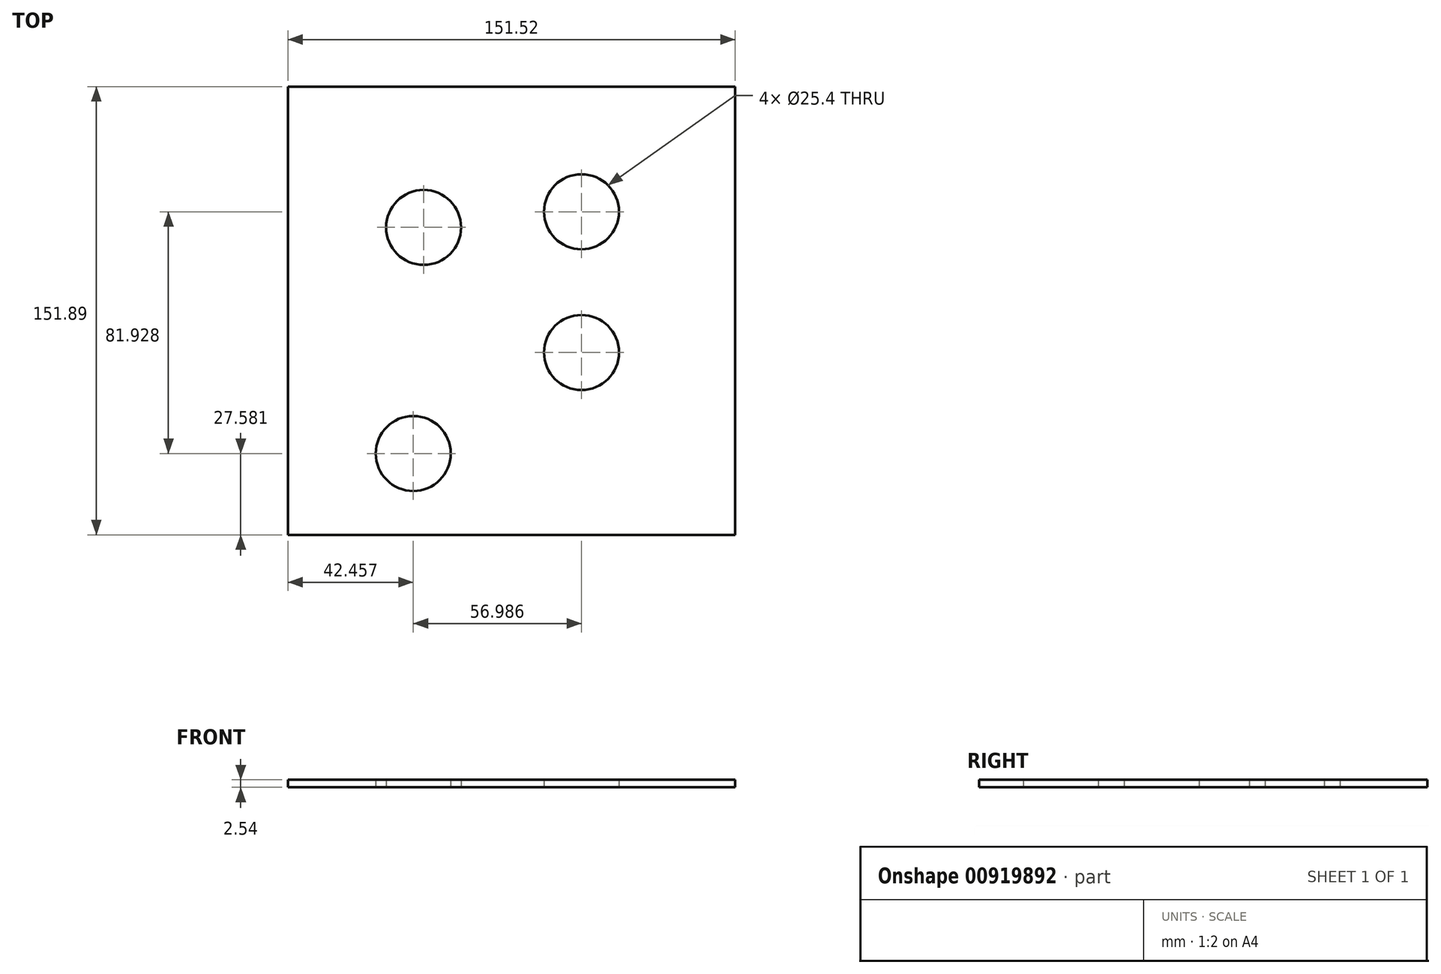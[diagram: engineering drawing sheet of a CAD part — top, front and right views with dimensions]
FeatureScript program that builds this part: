
annotation { "Feature Type Name" : "Feature", "Feature Type Description" : "" }
export const myFeature = defineFeature(function(context is Context, id is Id, definition is map)
    precondition{}
    {
        {
            var Q0;
            Q0=qCreatedBy(makeId("Top.planeOp"),FACE);
            var sketch = newSketch(context, id + "F0", { "sketchPlane" : qUnion([Q0])});
            skLineSegment(sketch, "E0.bottom", {"start": v(-75.39, 75.39) * mm, "end": v(76.13, 75.39) * mm});
            skLineSegment(sketch, "E0.top", {"start": v(-75.39, -76.5) * mm, "end": v(76.13, -76.5) * mm});
            skLineSegment(sketch, "E0.left", {"start": v(-75.39, 75.39) * mm, "end": v(-75.39, -76.5) * mm});
            skLineSegment(sketch, "E0.right", {"start": v(76.13, 75.39) * mm, "end": v(76.13, -76.5) * mm});
            skSolve(sketch);
        }
        {
            var Q0;
            Q0 = qSketchRegion(id + "F0", true);
            extrude(context, id + "F1", {"entities" : qUnion([Q0]), "depth" : 2.54 * mm, "offsetDistance" : 25.4 * mm});
        }
        {
            var Q0;
            Q0=makeQuery(id+"F1.opExtrude","CAP_FACE",FACE,{"disambiguationData":[OSD([sQuery(id+"F0.wireOp",EDGE,"E0.bottom"),sQuery(id+"F0.wireOp",EDGE,"E0.top"),sQuery(id+"F0.wireOp",EDGE,"E0.left"),sQuery(id+"F0.wireOp",EDGE,"E0.right")])],"isStart":true});
            var sketch = newSketch(context, id + "F2", { "sketchPlane" : qUnion([Q0])});
            skPoint(sketch, "E1", {"position": v(-32.93, 48.92) * mm});
            skPoint(sketch, "E2", {"position": v(24.05, 14.7) * mm});
            skPoint(sketch, "E3", {"position": v(24.05, -33) * mm});
            skPoint(sketch, "E4", {"position": v(-29.44, -27.69) * mm});
            skSolve(sketch);
        }
        {
            var Q0;
            Q0=sQuery(id+"F2.wireOp",VERTEX,"E4");
            var Q1;
            Q1=sQuery(id+"F2.wireOp",VERTEX,"E3");
            var Q2;
            Q2=sQuery(id+"F2.wireOp",VERTEX,"E2");
            var Q3;
            Q3=sQuery(id+"F2.wireOp",VERTEX,"E1");
            var Q4;
            Q4=makeQuery(id+"F1.opExtrude","SWEPT_BODY",BODY,{"disambiguationData":[OSD([sQuery(id+"F0.wireOp",EDGE,"E0.bottom"),sQuery(id+"F0.wireOp",EDGE,"E0.top"),sQuery(id+"F0.wireOp",EDGE,"E0.left"),sQuery(id+"F0.wireOp",EDGE,"E0.right")])]});
            hole(context, id + "F3", {"style" : HoleStyle.SIMPLE, "endStyle" : HoleEndStyle.THROUGH, "standardTappedOrClearance" : lookupTablePath({ "standard" : "Custom", "fit" : "Normal", "size" : "1/4", "type" : "Clearance" }), "standardBlindInLast" : lookupTablePath({ "fit" : "Normal", "standard" : "Custom", "size" : "1/4", "type" : "Clearance" }), "holeDiameter" : 25.4 * mm, "majorDiameter" : 6.35 * mm, "isTappedThrough" : true, "tappedDepth" : 12.7 * mm, "tapClearance" : 3, "locations" : qUnion([Q0, Q1, Q2, Q3]), "scope" : qUnion([Q4])});
        }
    });
